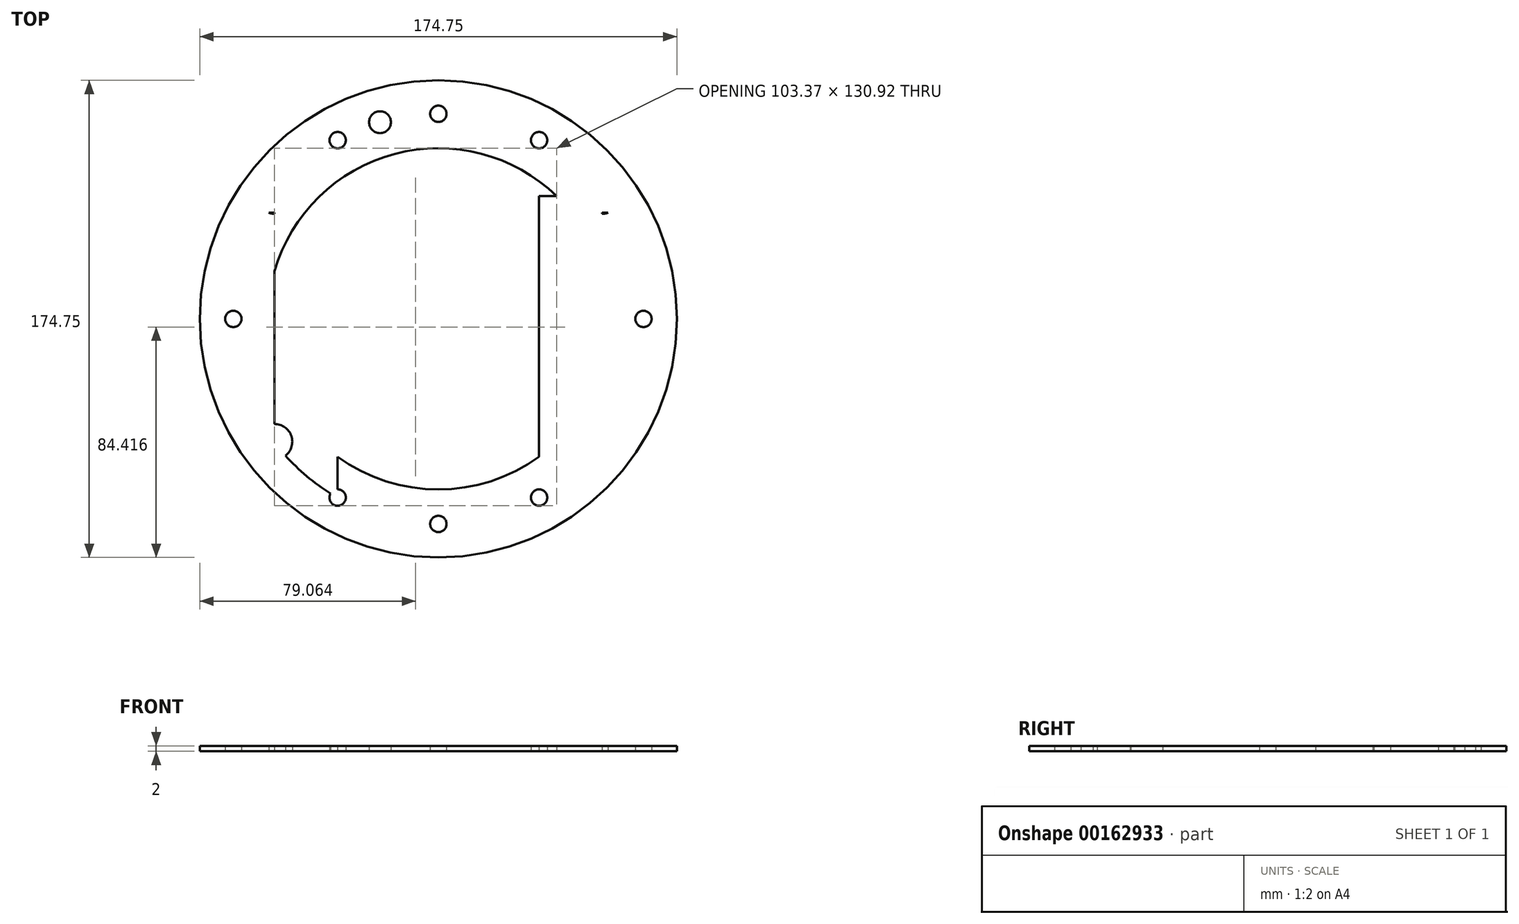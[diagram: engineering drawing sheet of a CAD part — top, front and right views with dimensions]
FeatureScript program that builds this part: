
annotation { "Feature Type Name" : "Feature", "Feature Type Description" : "" }
export const myFeature = defineFeature(function(context is Context, id is Id, definition is map)
    precondition{}
    {
        {
            var Q0;
            Q0=qCreatedBy(makeId("Top.planeOp"),FACE);
            var sketch = newSketch(context, id + "F0", { "sketchPlane" : qUnion([Q0])});
            skLineSegment(sketch, "E0.bottom", {"start": v(60.27, 43.84) * mm, "end": v(-59.73, 43.84) * mm});
            skLineSegment(sketch, "E0.top", {"start": v(60.27, -46.16) * mm, "end": v(-59.73, -46.16) * mm});
            skLineSegment(sketch, "E0.left", {"start": v(60.27, 43.84) * mm, "end": v(60.27, -46.16) * mm});
            skLineSegment(sketch, "E0.right", {"start": v(-59.73, 43.84) * mm, "end": v(-59.73, -46.16) * mm});
            skPoint(sketch, "E0.middle", {"position": v(0.27, -1.16) * mm});
            skCircle(sketch, "E1", {"center": v(60.27, 43.84) * mm, "radius": 6.5 * mm});
            skCircle(sketch, "E2", {"center": v(-59.73, 43.84) * mm, "radius": 6.5 * mm});
            skCircle(sketch, "E3", {"center": v(60.27, -46.16) * mm, "radius": 6.5 * mm});
            skCircle(sketch, "E4", {"center": v(-59.73, -46.16) * mm, "radius": 6.5 * mm});
            skCircle(sketch, "E5", {"center": v(0.27, -1.16) * mm, "radius": 87.38 * mm});
            skLineSegment(sketch, "E6.bottom", {"start": v(58.16, 49.99) * mm, "end": v(62.37, 49.99) * mm});
            skLineSegment(sketch, "E6.top", {"start": v(58.16, 37.69) * mm, "end": v(62.37, 37.69) * mm});
            skLineSegment(sketch, "E6.left", {"start": v(58.16, 49.99) * mm, "end": v(58.16, 37.69) * mm});
            skLineSegment(sketch, "E6.right", {"start": v(62.37, 49.99) * mm, "end": v(62.37, 37.69) * mm});
            skLineSegment(sketch, "E7.bottom", {"start": v(-61.84, 49.99) * mm, "end": v(-57.63, 49.99) * mm});
            skLineSegment(sketch, "E7.top", {"start": v(-61.84, 37.69) * mm, "end": v(-57.63, 37.69) * mm});
            skLineSegment(sketch, "E7.left", {"start": v(-61.84, 49.99) * mm, "end": v(-61.84, 37.69) * mm});
            skLineSegment(sketch, "E7.right", {"start": v(-57.63, 49.99) * mm, "end": v(-57.63, 37.69) * mm});
            skLineSegment(sketch, "E8.bottom", {"start": v(62.37, -40.01) * mm, "end": v(58.16, -40.01) * mm});
            skLineSegment(sketch, "E8.top", {"start": v(62.37, -52.31) * mm, "end": v(58.16, -52.31) * mm});
            skLineSegment(sketch, "E8.left", {"start": v(62.37, -40.01) * mm, "end": v(62.37, -52.31) * mm});
            skLineSegment(sketch, "E8.right", {"start": v(58.16, -40.01) * mm, "end": v(58.16, -52.31) * mm});
            skLineSegment(sketch, "E9.bottom", {"start": v(-61.84, -40.01) * mm, "end": v(-57.63, -40.01) * mm});
            skLineSegment(sketch, "E9.top", {"start": v(-61.84, -52.31) * mm, "end": v(-57.63, -52.31) * mm});
            skLineSegment(sketch, "E9.left", {"start": v(-61.84, -40.01) * mm, "end": v(-61.84, -52.31) * mm});
            skLineSegment(sketch, "E9.right", {"start": v(-57.63, -40.01) * mm, "end": v(-57.63, -52.31) * mm});
            skLineSegment(sketch, "E10.bottom", {"start": v(58.16, -40.01) * mm, "end": v(80.94, -40.01) * mm});
            skLineSegment(sketch, "E10.top", {"start": v(58.16, -52.31) * mm, "end": v(80.94, -52.31) * mm});
            skLineSegment(sketch, "E10.right", {"start": v(80.94, -40.01) * mm, "end": v(80.94, -52.31) * mm});
            skLineSegment(sketch, "E11.bottom", {"start": v(58.16, 49.99) * mm, "end": v(78.53, 49.99) * mm});
            skLineSegment(sketch, "E11.top", {"start": v(58.16, 37.69) * mm, "end": v(78.53, 37.69) * mm});
            skLineSegment(sketch, "E11.right", {"start": v(78.53, 49.99) * mm, "end": v(78.53, 37.69) * mm});
            skLineSegment(sketch, "E12.bottom", {"start": v(-57.63, 49.99) * mm, "end": v(-78, 49.99) * mm});
            skLineSegment(sketch, "E12.top", {"start": v(-57.63, 37.69) * mm, "end": v(-78, 37.69) * mm});
            skLineSegment(sketch, "E12.right", {"start": v(-78, 49.99) * mm, "end": v(-78, 37.69) * mm});
            skLineSegment(sketch, "E13.bottom", {"start": v(-57.63, -40.01) * mm, "end": v(-78, -40.01) * mm});
            skLineSegment(sketch, "E13.top", {"start": v(-57.63, -52.31) * mm, "end": v(-78, -52.31) * mm});
            skLineSegment(sketch, "E13.right", {"start": v(-78, -40.01) * mm, "end": v(-78, -52.31) * mm});
            skCircle(sketch, "E14", {"center": v(0.27, 73.95) * mm, "radius": 3 * mm});
            skCircle(sketch, "E15", {"center": v(0.27, -76.28) * mm, "radius": 3 * mm});
            skCircle(sketch, "E16", {"center": v(75.38, -1.16) * mm, "radius": 3 * mm});
            skCircle(sketch, "E17", {"center": v(-74.85, -1.16) * mm, "radius": 3 * mm});
            skCircle(sketch, "E18", {"center": v(-21.11, 70.87) * mm, "radius": 4 * mm});
            skCircle(sketch, "E19", {"center": v(0.27, -1.16) * mm, "radius": 75.13 * mm});
            skLineSegment(sketch, "E20.bottom", {"start": v(37.16, 64.3) * mm, "end": v(-36.63, 64.3) * mm});
            skLineSegment(sketch, "E20.top", {"start": v(37.16, -66.61) * mm, "end": v(-36.63, -66.61) * mm});
            skLineSegment(sketch, "E20.left", {"start": v(37.16, 64.3) * mm, "end": v(37.16, -66.61) * mm});
            skLineSegment(sketch, "E20.right", {"start": v(-36.63, 64.3) * mm, "end": v(-36.63, -66.61) * mm});
            skCircle(sketch, "E21", {"center": v(-36.63, 64.3) * mm, "radius": 3 * mm});
            skCircle(sketch, "E22", {"center": v(37.16, 64.3) * mm, "radius": 3 * mm});
            skCircle(sketch, "E23", {"center": v(37.16, -66.61) * mm, "radius": 3 * mm});
            skCircle(sketch, "E24", {"center": v(-36.63, -66.61) * mm, "radius": 3 * mm});
            skCircle(sketch, "E25", {"center": v(0.27, -1.16) * mm, "radius": 62.5 * mm});
            skSolve(sketch);
        }
        {
            var Q0;
            {var subQ0=sQuery(id+"F0.wireOp",EDGE,"E11.bottom");var subQ3=sQuery(id+"F0.wireOp",EDGE,"E5");var subQ4=makeQuery(id+"F0.imprint","INTERSECT",VERTEX,{"derivedFrom":[subQ3,subQ0]});Q0=makeQuery(id+"F0.imprint","IMPRINT",FACE,{"disambiguationData":[TD([[makeQuery(id+"F0.imprint","IMPRINT",EDGE,{"disambiguationData":[TD([[subQ4,-1.0]])],"derivedFrom":subQ3}),1.0]])]});}
            var Q1;
            {var subQ0=sQuery(id+"F0.wireOp",EDGE,"E19");var subQ1=sQuery(id+"F0.wireOp",EDGE,"E14");var subQ5=makeQuery(id+"F0.imprint","INTERSECT",VERTEX,{"disambiguationData":[OD(0.0)],"derivedFrom":[subQ1,subQ0]});Q1=makeQuery(id+"F0.imprint","IMPRINT",FACE,{"disambiguationData":[TD([[makeQuery(id+"F0.imprint","IMPRINT",EDGE,{"disambiguationData":[TD([[subQ5,1.0]])],"derivedFrom":subQ1}),-1.0]])]});}
            var Q2;
            {var subQ0=sQuery(id+"F0.wireOp",EDGE,"E20.left");var subQ1=sQuery(id+"F0.wireOp",EDGE,"b08183dc-c876-4888-9f75-b60d98332972");var subQ2=makeQuery(id+"F0.imprint","INTERSECT",VERTEX,{"disambiguationData":[OD(0.0)],"derivedFrom":[subQ1,subQ0]});Q2=makeQuery(id+"F0.imprint","IMPRINT",FACE,{"disambiguationData":[TD([[makeQuery(id+"F0.imprint","IMPRINT",EDGE,{"disambiguationData":[TD([[subQ2,-1.0]])],"derivedFrom":subQ1}),-1.0]])]});}
            var Q3;
            {var subQ1=sQuery(id+"F0.wireOp",EDGE,"E1");var subQ6=sQuery(id+"F0.wireOp",EDGE,"E0.bottom");var subQ10=makeQuery(id+"F0.imprint","INTERSECT",VERTEX,{"derivedFrom":[subQ6,subQ1]});Q3=makeQuery(id+"F0.imprint","IMPRINT",FACE,{"disambiguationData":[TD([[makeQuery(id+"F0.imprint","IMPRINT",EDGE,{"disambiguationData":[TD([[subQ10,-1.0]])],"derivedFrom":subQ6}),-1.0]])]});}
            var Q4;
            {var subQ0=sQuery(id+"F0.wireOp",EDGE,"b08183dc-c876-4888-9f75-b60d98332972");var subQ1=sQuery(id+"F0.wireOp",EDGE,"E0.bottom");var subQ2=makeQuery(id+"F0.imprint","INTERSECT",VERTEX,{"disambiguationData":[OD(1.0)],"derivedFrom":[subQ1,subQ0]});Q4=makeQuery(id+"F0.imprint","IMPRINT",FACE,{"disambiguationData":[TD([[makeQuery(id+"F0.imprint","IMPRINT",EDGE,{"disambiguationData":[TD([[subQ2,-1.0]])],"derivedFrom":subQ1}),-1.0]])]});}
            var Q5;
            {var subQ3=sQuery(id+"F0.wireOp",EDGE,"E0.right");var subQ5=sQuery(id+"F0.wireOp",EDGE,"E2");var subQ6=makeQuery(id+"F0.imprint","INTERSECT",VERTEX,{"derivedFrom":[subQ3,subQ5]});Q5=makeQuery(id+"F0.imprint","IMPRINT",FACE,{"disambiguationData":[TD([[makeQuery(id+"F0.imprint","IMPRINT",EDGE,{"disambiguationData":[TD([[subQ6,-1.0]])],"derivedFrom":subQ3}),-1.0]])]});}
            var Q6;
            {var subQ2=sQuery(id+"F0.wireOp",EDGE,"E0.bottom");var subQ6=sQuery(id+"F0.wireOp",EDGE,"b08183dc-c876-4888-9f75-b60d98332972");var subQ8=makeQuery(id+"F0.imprint","INTERSECT",VERTEX,{"disambiguationData":[OD(1.0)],"derivedFrom":[subQ2,subQ6]});Q6=makeQuery(id+"F0.imprint","IMPRINT",FACE,{"disambiguationData":[TD([[makeQuery(id+"F0.imprint","IMPRINT",EDGE,{"disambiguationData":[TD([[subQ8,-1.0]])],"derivedFrom":subQ2}),1.0]])]});}
            var Q7;
            {var subQ3=sQuery(id+"F0.wireOp",EDGE,"E19");var subQ7=sQuery(id+"F0.wireOp",EDGE,"E2");var subQ9=makeQuery(id+"F0.imprint","INTERSECT",VERTEX,{"disambiguationData":[OD(1.0)],"derivedFrom":[subQ7,subQ3]});Q7=makeQuery(id+"F0.imprint","IMPRINT",FACE,{"disambiguationData":[TD([[makeQuery(id+"F0.imprint","IMPRINT",EDGE,{"disambiguationData":[TD([[subQ9,-1.0]])],"derivedFrom":subQ3}),-1.0]])]});}
            var Q8;
            {var subQ1=sQuery(id+"F0.wireOp",EDGE,"E2");var subQ3=sQuery(id+"F0.wireOp",EDGE,"E19");var subQ4=makeQuery(id+"F0.imprint","INTERSECT",VERTEX,{"disambiguationData":[OD(1.0)],"derivedFrom":[subQ1,subQ3]});Q8=makeQuery(id+"F0.imprint","IMPRINT",FACE,{"disambiguationData":[TD([[makeQuery(id+"F0.imprint","IMPRINT",EDGE,{"disambiguationData":[TD([[subQ4,1.0]])],"derivedFrom":subQ3}),-1.0]])]});}
            var Q9;
            {var subQ1=sQuery(id+"F0.wireOp",EDGE,"E7.left");var subQ4=sQuery(id+"F0.wireOp",EDGE,"E19");var subQ5=makeQuery(id+"F0.imprint","INTERSECT",VERTEX,{"derivedFrom":[subQ1,subQ4]});Q9=makeQuery(id+"F0.imprint","IMPRINT",FACE,{"disambiguationData":[TD([[makeQuery(id+"F0.imprint","IMPRINT",EDGE,{"disambiguationData":[TD([[subQ5,1.0]])],"derivedFrom":subQ4}),-1.0]])]});}
            var Q10;
            {var subQ0=sQuery(id+"F0.wireOp",EDGE,"E2");var subQ1=sQuery(id+"F0.wireOp",EDGE,"E0.bottom");var subQ2=makeQuery(id+"F0.imprint","INTERSECT",VERTEX,{"derivedFrom":[subQ1,subQ0]});Q10=makeQuery(id+"F0.imprint","IMPRINT",FACE,{"disambiguationData":[TD([[makeQuery(id+"F0.imprint","IMPRINT",EDGE,{"disambiguationData":[TD([[subQ2,-1.0]])],"derivedFrom":subQ1}),-1.0]])]});}
            var Q11;
            {var subQ1=sQuery(id+"F0.wireOp",EDGE,"E2");var subQ3=sQuery(id+"F0.wireOp",EDGE,"E19");var subQ4=makeQuery(id+"F0.imprint","INTERSECT",VERTEX,{"disambiguationData":[OD(0.0)],"derivedFrom":[subQ1,subQ3]});Q11=makeQuery(id+"F0.imprint","IMPRINT",FACE,{"disambiguationData":[TD([[makeQuery(id+"F0.imprint","IMPRINT",EDGE,{"disambiguationData":[TD([[subQ4,-1.0]])],"derivedFrom":subQ3}),-1.0]])]});}
            var Q12;
            {var subQ0=sQuery(id+"F0.wireOp",EDGE,"E12.bottom");var subQ1=sQuery(id+"F0.wireOp",EDGE,"E2");var subQ2=makeQuery(id+"F0.imprint","INTERSECT",VERTEX,{"derivedFrom":[subQ1,sQuery(id+"F0.wireOp",EDGE,"E7.left"),subQ0]});Q12=makeQuery(id+"F0.imprint","IMPRINT",FACE,{"disambiguationData":[TD([[makeQuery(id+"F0.imprint","IMPRINT",EDGE,{"disambiguationData":[TD([[subQ2,1.0]])],"derivedFrom":subQ1}),1.0]])]});}
            var Q13;
            {var subQ3=sQuery(id+"F0.wireOp",EDGE,"E0.right");var subQ9=sQuery(id+"F0.wireOp",EDGE,"E0.bottom");var subQ10=makeQuery(id+"F0.imprint","INTERSECT",VERTEX,{"derivedFrom":[subQ9,subQ3]});Q13=makeQuery(id+"F0.imprint","IMPRINT",FACE,{"disambiguationData":[TD([[makeQuery(id+"F0.imprint","IMPRINT",EDGE,{"disambiguationData":[TD([[subQ10,1.0]])],"derivedFrom":subQ9}),-1.0]])]});}
            var Q14;
            {var subQ0=sQuery(id+"F0.wireOp",EDGE,"E0.right");var subQ1=sQuery(id+"F0.wireOp",EDGE,"E0.bottom");var subQ2=makeQuery(id+"F0.imprint","INTERSECT",VERTEX,{"derivedFrom":[subQ1,subQ0]});Q14=makeQuery(id+"F0.imprint","IMPRINT",FACE,{"disambiguationData":[TD([[makeQuery(id+"F0.imprint","IMPRINT",EDGE,{"disambiguationData":[TD([[subQ2,1.0]])],"derivedFrom":subQ1}),1.0]])]});}
            var Q15;
            {var subQ0=sQuery(id+"F0.wireOp",EDGE,"E2");var subQ1=sQuery(id+"F0.wireOp",EDGE,"E0.bottom");var subQ2=makeQuery(id+"F0.imprint","INTERSECT",VERTEX,{"derivedFrom":[subQ1,subQ0]});Q15=makeQuery(id+"F0.imprint","IMPRINT",FACE,{"disambiguationData":[TD([[makeQuery(id+"F0.imprint","IMPRINT",EDGE,{"disambiguationData":[TD([[subQ2,-1.0]])],"derivedFrom":subQ1}),1.0]])]});}
            var Q16;
            {var subQ0=sQuery(id+"F0.wireOp",EDGE,"E12.top");var subQ1=sQuery(id+"F0.wireOp",EDGE,"E0.right");var subQ2=makeQuery(id+"F0.imprint","INTERSECT",VERTEX,{"derivedFrom":[subQ1,subQ0]});Q16=makeQuery(id+"F0.imprint","IMPRINT",FACE,{"disambiguationData":[TD([[makeQuery(id+"F0.imprint","IMPRINT",EDGE,{"disambiguationData":[TD([[subQ2,-1.0]])],"derivedFrom":subQ1}),1.0]])]});}
            var Q17;
            {var subQ0=sQuery(id+"F0.wireOp",EDGE,"E12.top");var subQ1=sQuery(id+"F0.wireOp",EDGE,"E0.right");var subQ2=makeQuery(id+"F0.imprint","INTERSECT",VERTEX,{"derivedFrom":[subQ1,subQ0]});Q17=makeQuery(id+"F0.imprint","IMPRINT",FACE,{"disambiguationData":[TD([[makeQuery(id+"F0.imprint","IMPRINT",EDGE,{"disambiguationData":[TD([[subQ2,-1.0]])],"derivedFrom":subQ1}),-1.0]])]});}
            var Q18;
            {var subQ1=sQuery(id+"F0.wireOp",EDGE,"E2");var subQ3=sQuery(id+"F0.wireOp",EDGE,"E19");var subQ4=makeQuery(id+"F0.imprint","INTERSECT",VERTEX,{"disambiguationData":[OD(1.0)],"derivedFrom":[subQ1,subQ3]});Q18=makeQuery(id+"F0.imprint","IMPRINT",FACE,{"disambiguationData":[TD([[makeQuery(id+"F0.imprint","IMPRINT",EDGE,{"disambiguationData":[TD([[subQ4,1.0]])],"derivedFrom":subQ3}),1.0]])]});}
            var Q19;
            {var subQ1=sQuery(id+"F0.wireOp",EDGE,"E2");var subQ3=sQuery(id+"F0.wireOp",EDGE,"E19");var subQ4=makeQuery(id+"F0.imprint","INTERSECT",VERTEX,{"disambiguationData":[OD(1.0)],"derivedFrom":[subQ1,subQ3]});Q19=makeQuery(id+"F0.imprint","IMPRINT",FACE,{"disambiguationData":[TD([[makeQuery(id+"F0.imprint","IMPRINT",EDGE,{"disambiguationData":[TD([[subQ4,-1.0]])],"derivedFrom":subQ3}),1.0]])]});}
            var Q20;
            {var subQ0=sQuery(id+"F0.wireOp",EDGE,"E13.right");var subQ1=sQuery(id+"F0.wireOp",EDGE,"E13.bottom");var subQ2=makeQuery(id+"F0.imprint","INTERSECT",VERTEX,{"derivedFrom":[subQ1,subQ0]});Q20=makeQuery(id+"F0.imprint","IMPRINT",FACE,{"disambiguationData":[TD([[makeQuery(id+"F0.imprint","IMPRINT",EDGE,{"disambiguationData":[TD([[subQ2,1.0]])],"derivedFrom":subQ1}),-1.0]])]});}
            var Q21;
            {var subQ0=sQuery(id+"F0.wireOp",EDGE,"E11.bottom");var subQ1=sQuery(id+"F0.wireOp",EDGE,"E1");var subQ2=makeQuery(id+"F0.imprint","INTERSECT",VERTEX,{"derivedFrom":[subQ1,sQuery(id+"F0.wireOp",EDGE,"E6.right"),subQ0]});Q21=makeQuery(id+"F0.imprint","IMPRINT",FACE,{"disambiguationData":[TD([[makeQuery(id+"F0.imprint","IMPRINT",EDGE,{"disambiguationData":[TD([[subQ2,-1.0]])],"derivedFrom":subQ1}),1.0]])]});}
            var Q22;
            {var subQ1=sQuery(id+"F0.wireOp",EDGE,"E1");var subQ3=sQuery(id+"F0.wireOp",EDGE,"E19");var subQ4=makeQuery(id+"F0.imprint","INTERSECT",VERTEX,{"disambiguationData":[OD(0.0)],"derivedFrom":[subQ1,subQ3]});Q22=makeQuery(id+"F0.imprint","IMPRINT",FACE,{"disambiguationData":[TD([[makeQuery(id+"F0.imprint","IMPRINT",EDGE,{"disambiguationData":[TD([[subQ4,1.0]])],"derivedFrom":subQ3}),-1.0]])]});}
            var Q23;
            {var subQ0=sQuery(id+"F0.wireOp",EDGE,"E6.left");var subQ1=sQuery(id+"F0.wireOp",EDGE,"E0.bottom");var subQ2=makeQuery(id+"F0.imprint","INTERSECT",VERTEX,{"derivedFrom":[subQ1,subQ0]});Q23=makeQuery(id+"F0.imprint","IMPRINT",FACE,{"disambiguationData":[TD([[makeQuery(id+"F0.imprint","IMPRINT",EDGE,{"disambiguationData":[TD([[subQ2,-1.0]])],"derivedFrom":subQ1}),-1.0]])]});}
            var Q24;
            {var subQ0=sQuery(id+"F0.wireOp",EDGE,"E6.left");var subQ1=sQuery(id+"F0.wireOp",EDGE,"E0.bottom");var subQ2=makeQuery(id+"F0.imprint","INTERSECT",VERTEX,{"derivedFrom":[subQ1,subQ0]});Q24=makeQuery(id+"F0.imprint","IMPRINT",FACE,{"disambiguationData":[TD([[makeQuery(id+"F0.imprint","IMPRINT",EDGE,{"disambiguationData":[TD([[subQ2,-1.0]])],"derivedFrom":subQ1}),1.0]])]});}
            var Q25;
            {var subQ3=sQuery(id+"F0.wireOp",EDGE,"E0.left");var subQ7=sQuery(id+"F0.wireOp",EDGE,"E0.bottom");var subQ8=makeQuery(id+"F0.imprint","INTERSECT",VERTEX,{"derivedFrom":[subQ7,subQ3]});Q25=makeQuery(id+"F0.imprint","IMPRINT",FACE,{"disambiguationData":[TD([[makeQuery(id+"F0.imprint","IMPRINT",EDGE,{"disambiguationData":[TD([[subQ8,-1.0]])],"derivedFrom":subQ7}),-1.0]])]});}
            var Q26;
            {var subQ0=sQuery(id+"F0.wireOp",EDGE,"E0.left");var subQ1=sQuery(id+"F0.wireOp",EDGE,"E0.bottom");var subQ2=makeQuery(id+"F0.imprint","INTERSECT",VERTEX,{"derivedFrom":[subQ1,subQ0]});Q26=makeQuery(id+"F0.imprint","IMPRINT",FACE,{"disambiguationData":[TD([[makeQuery(id+"F0.imprint","IMPRINT",EDGE,{"disambiguationData":[TD([[subQ2,-1.0]])],"derivedFrom":subQ1}),1.0]])]});}
            var Q27;
            {var subQ1=sQuery(id+"F0.wireOp",EDGE,"E6.right");var subQ4=sQuery(id+"F0.wireOp",EDGE,"E19");var subQ5=makeQuery(id+"F0.imprint","INTERSECT",VERTEX,{"derivedFrom":[subQ1,subQ4]});Q27=makeQuery(id+"F0.imprint","IMPRINT",FACE,{"disambiguationData":[TD([[makeQuery(id+"F0.imprint","IMPRINT",EDGE,{"disambiguationData":[TD([[subQ5,-1.0]])],"derivedFrom":subQ4}),-1.0]])]});}
            var Q28;
            {var subQ1=sQuery(id+"F0.wireOp",EDGE,"E1");var subQ3=sQuery(id+"F0.wireOp",EDGE,"E19");var subQ4=makeQuery(id+"F0.imprint","INTERSECT",VERTEX,{"disambiguationData":[OD(1.0)],"derivedFrom":[subQ1,subQ3]});Q28=makeQuery(id+"F0.imprint","IMPRINT",FACE,{"disambiguationData":[TD([[makeQuery(id+"F0.imprint","IMPRINT",EDGE,{"disambiguationData":[TD([[subQ4,-1.0]])],"derivedFrom":subQ3}),-1.0]])]});}
            var Q29;
            {var subQ1=sQuery(id+"F0.wireOp",EDGE,"E1");var subQ3=sQuery(id+"F0.wireOp",EDGE,"E19");var subQ4=makeQuery(id+"F0.imprint","INTERSECT",VERTEX,{"disambiguationData":[OD(1.0)],"derivedFrom":[subQ1,subQ3]});Q29=makeQuery(id+"F0.imprint","IMPRINT",FACE,{"disambiguationData":[TD([[makeQuery(id+"F0.imprint","IMPRINT",EDGE,{"disambiguationData":[TD([[subQ4,-1.0]])],"derivedFrom":subQ3}),1.0]])]});}
            var Q30;
            {var subQ0=sQuery(id+"F0.wireOp",EDGE,"E11.top");var subQ1=sQuery(id+"F0.wireOp",EDGE,"E0.left");var subQ2=makeQuery(id+"F0.imprint","INTERSECT",VERTEX,{"derivedFrom":[subQ1,subQ0]});Q30=makeQuery(id+"F0.imprint","IMPRINT",FACE,{"disambiguationData":[TD([[makeQuery(id+"F0.imprint","IMPRINT",EDGE,{"disambiguationData":[TD([[subQ2,-1.0]])],"derivedFrom":subQ1}),1.0]])]});}
            var Q31;
            {var subQ0=sQuery(id+"F0.wireOp",EDGE,"E11.top");var subQ1=sQuery(id+"F0.wireOp",EDGE,"E0.left");var subQ2=makeQuery(id+"F0.imprint","INTERSECT",VERTEX,{"derivedFrom":[subQ1,subQ0]});Q31=makeQuery(id+"F0.imprint","IMPRINT",FACE,{"disambiguationData":[TD([[makeQuery(id+"F0.imprint","IMPRINT",EDGE,{"disambiguationData":[TD([[subQ2,-1.0]])],"derivedFrom":subQ1}),-1.0]])]});}
            var Q32;
            {var subQ1=sQuery(id+"F0.wireOp",EDGE,"E1");var subQ3=sQuery(id+"F0.wireOp",EDGE,"E19");var subQ4=makeQuery(id+"F0.imprint","INTERSECT",VERTEX,{"disambiguationData":[OD(1.0)],"derivedFrom":[subQ1,subQ3]});Q32=makeQuery(id+"F0.imprint","IMPRINT",FACE,{"disambiguationData":[TD([[makeQuery(id+"F0.imprint","IMPRINT",EDGE,{"disambiguationData":[TD([[subQ4,1.0]])],"derivedFrom":subQ3}),1.0]])]});}
            var Q33;
            {var subQ1=sQuery(id+"F0.wireOp",EDGE,"E1");var subQ7=sQuery(id+"F0.wireOp",EDGE,"E19");var subQ9=makeQuery(id+"F0.imprint","INTERSECT",VERTEX,{"disambiguationData":[OD(1.0)],"derivedFrom":[subQ1,subQ7]});Q33=makeQuery(id+"F0.imprint","IMPRINT",FACE,{"disambiguationData":[TD([[makeQuery(id+"F0.imprint","IMPRINT",EDGE,{"disambiguationData":[TD([[subQ9,1.0]])],"derivedFrom":subQ7}),-1.0]])]});}
            var Q34;
            {var subQ0=sQuery(id+"F0.wireOp",EDGE,"E1");var subQ4=sQuery(id+"F0.wireOp",EDGE,"E0.bottom");var subQ5=makeQuery(id+"F0.imprint","INTERSECT",VERTEX,{"derivedFrom":[subQ4,subQ0]});Q34=makeQuery(id+"F0.imprint","IMPRINT",FACE,{"disambiguationData":[TD([[makeQuery(id+"F0.imprint","IMPRINT",EDGE,{"disambiguationData":[TD([[subQ5,-1.0]])],"derivedFrom":subQ4}),1.0]])]});}
            var Q35;
            {var subQ3=sQuery(id+"F0.wireOp",EDGE,"E0.left");var subQ6=sQuery(id+"F0.wireOp",EDGE,"E1");var subQ8=makeQuery(id+"F0.imprint","INTERSECT",VERTEX,{"derivedFrom":[subQ3,subQ6]});Q35=makeQuery(id+"F0.imprint","IMPRINT",FACE,{"disambiguationData":[TD([[makeQuery(id+"F0.imprint","IMPRINT",EDGE,{"disambiguationData":[TD([[subQ8,-1.0]])],"derivedFrom":subQ3}),1.0]])]});}
            var Q36;
            {var subQ5=sQuery(id+"F0.wireOp",EDGE,"E5");var subQ8=sQuery(id+"F0.wireOp",EDGE,"E10.bottom");var subQ9=makeQuery(id+"F0.imprint","INTERSECT",VERTEX,{"derivedFrom":[subQ5,subQ8]});Q36=makeQuery(id+"F0.imprint","IMPRINT",FACE,{"disambiguationData":[TD([[makeQuery(id+"F0.imprint","IMPRINT",EDGE,{"disambiguationData":[TD([[subQ9,1.0]])],"derivedFrom":subQ8}),1.0]])]});}
            var Q37;
            {var subQ2=sQuery(id+"F0.wireOp",EDGE,"E0.top");var subQ6=sQuery(id+"F0.wireOp",EDGE,"b08183dc-c876-4888-9f75-b60d98332972");var subQ8=makeQuery(id+"F0.imprint","INTERSECT",VERTEX,{"disambiguationData":[OD(1.0)],"derivedFrom":[subQ2,subQ6]});Q37=makeQuery(id+"F0.imprint","IMPRINT",FACE,{"disambiguationData":[TD([[makeQuery(id+"F0.imprint","IMPRINT",EDGE,{"disambiguationData":[TD([[subQ8,-1.0]])],"derivedFrom":subQ2}),-1.0]])]});}
            var Q38;
            {var subQ0=sQuery(id+"F0.wireOp",EDGE,"b08183dc-c876-4888-9f75-b60d98332972");var subQ1=sQuery(id+"F0.wireOp",EDGE,"E0.top");var subQ2=makeQuery(id+"F0.imprint","INTERSECT",VERTEX,{"disambiguationData":[OD(1.0)],"derivedFrom":[subQ1,subQ0]});Q38=makeQuery(id+"F0.imprint","IMPRINT",FACE,{"disambiguationData":[TD([[makeQuery(id+"F0.imprint","IMPRINT",EDGE,{"disambiguationData":[TD([[subQ2,-1.0]])],"derivedFrom":subQ1}),1.0]])]});}
            var Q39;
            {var subQ1=sQuery(id+"F0.wireOp",EDGE,"b08183dc-c876-4888-9f75-b60d98332972");var subQ5=sQuery(id+"F0.wireOp",EDGE,"E20.right");var subQ6=makeQuery(id+"F0.imprint","INTERSECT",VERTEX,{"disambiguationData":[OD(1.0)],"derivedFrom":[subQ1,subQ5]});Q39=makeQuery(id+"F0.imprint","IMPRINT",FACE,{"disambiguationData":[TD([[makeQuery(id+"F0.imprint","IMPRINT",EDGE,{"disambiguationData":[TD([[subQ6,-1.0]])],"derivedFrom":subQ1}),-1.0]])]});}
            var Q40;
            {var subQ1=sQuery(id+"F0.wireOp",EDGE,"E3");var subQ6=sQuery(id+"F0.wireOp",EDGE,"E0.top");var subQ10=makeQuery(id+"F0.imprint","INTERSECT",VERTEX,{"derivedFrom":[subQ6,subQ1]});Q40=makeQuery(id+"F0.imprint","IMPRINT",FACE,{"disambiguationData":[TD([[makeQuery(id+"F0.imprint","IMPRINT",EDGE,{"disambiguationData":[TD([[subQ10,-1.0]])],"derivedFrom":subQ6}),1.0]])]});}
            var Q41;
            {var subQ0=sQuery(id+"F0.wireOp",EDGE,"E3");var subQ2=sQuery(id+"F0.wireOp",EDGE,"E0.top");var subQ3=makeQuery(id+"F0.imprint","INTERSECT",VERTEX,{"derivedFrom":[subQ2,subQ0]});Q41=makeQuery(id+"F0.imprint","IMPRINT",FACE,{"disambiguationData":[TD([[makeQuery(id+"F0.imprint","IMPRINT",EDGE,{"disambiguationData":[TD([[subQ3,-1.0]])],"derivedFrom":subQ2}),-1.0]])]});}
            var Q42;
            {var subQ13=sQuery(id+"F0.wireOp",EDGE,"E13.top");var subQ15=sQuery(id+"F0.wireOp",EDGE,"E5");var subQ16=makeQuery(id+"F0.imprint","INTERSECT",VERTEX,{"derivedFrom":[subQ15,subQ13]});Q42=makeQuery(id+"F0.imprint","IMPRINT",FACE,{"disambiguationData":[TD([[makeQuery(id+"F0.imprint","IMPRINT",EDGE,{"disambiguationData":[TD([[subQ16,-1.0]])],"derivedFrom":subQ15}),1.0]])]});}
            var Q43;
            {var subQ5=sQuery(id+"F0.wireOp",EDGE,"E19");var subQ7=sQuery(id+"F0.wireOp",EDGE,"E15");var subQ10=makeQuery(id+"F0.imprint","INTERSECT",VERTEX,{"disambiguationData":[OD(0.0)],"derivedFrom":[subQ7,subQ5]});Q43=makeQuery(id+"F0.imprint","IMPRINT",FACE,{"disambiguationData":[TD([[makeQuery(id+"F0.imprint","IMPRINT",EDGE,{"disambiguationData":[TD([[subQ10,1.0]])],"derivedFrom":subQ7}),-1.0]])]});}
            var Q44;
            {var subQ3=sQuery(id+"F0.wireOp",EDGE,"E5");var subQ5=sQuery(id+"F0.wireOp",EDGE,"E13.right");var subQ6=makeQuery(id+"F0.imprint","INTERSECT",VERTEX,{"derivedFrom":[subQ3,subQ5]});Q44=makeQuery(id+"F0.imprint","IMPRINT",FACE,{"disambiguationData":[TD([[makeQuery(id+"F0.imprint","IMPRINT",EDGE,{"disambiguationData":[TD([[subQ6,-1.0]])],"derivedFrom":subQ3}),1.0]])]});}
            var Q45;
            {var subQ1=sQuery(id+"F0.wireOp",EDGE,"E4");var subQ3=sQuery(id+"F0.wireOp",EDGE,"E19");var subQ4=makeQuery(id+"F0.imprint","INTERSECT",VERTEX,{"disambiguationData":[OD(0.0)],"derivedFrom":[subQ1,subQ3]});Q45=makeQuery(id+"F0.imprint","IMPRINT",FACE,{"disambiguationData":[TD([[makeQuery(id+"F0.imprint","IMPRINT",EDGE,{"disambiguationData":[TD([[subQ4,-1.0]])],"derivedFrom":subQ3}),-1.0]])]});}
            var Q46;
            {var subQ1=sQuery(id+"F0.wireOp",EDGE,"E9.left");var subQ4=sQuery(id+"F0.wireOp",EDGE,"E19");var subQ5=makeQuery(id+"F0.imprint","INTERSECT",VERTEX,{"derivedFrom":[subQ1,subQ4]});Q46=makeQuery(id+"F0.imprint","IMPRINT",FACE,{"disambiguationData":[TD([[makeQuery(id+"F0.imprint","IMPRINT",EDGE,{"disambiguationData":[TD([[subQ5,-1.0]])],"derivedFrom":subQ4}),-1.0]])]});}
            var Q47;
            {var subQ0=sQuery(id+"F0.wireOp",EDGE,"E13.top");var subQ1=sQuery(id+"F0.wireOp",EDGE,"E4");var subQ2=makeQuery(id+"F0.imprint","INTERSECT",VERTEX,{"derivedFrom":[subQ1,sQuery(id+"F0.wireOp",EDGE,"E9.left"),subQ0]});Q47=makeQuery(id+"F0.imprint","IMPRINT",FACE,{"disambiguationData":[TD([[makeQuery(id+"F0.imprint","IMPRINT",EDGE,{"disambiguationData":[TD([[subQ2,-1.0]])],"derivedFrom":subQ1}),1.0]])]});}
            var Q48;
            {var subQ1=sQuery(id+"F0.wireOp",EDGE,"E4");var subQ3=sQuery(id+"F0.wireOp",EDGE,"E19");var subQ4=makeQuery(id+"F0.imprint","INTERSECT",VERTEX,{"disambiguationData":[OD(1.0)],"derivedFrom":[subQ1,subQ3]});Q48=makeQuery(id+"F0.imprint","IMPRINT",FACE,{"disambiguationData":[TD([[makeQuery(id+"F0.imprint","IMPRINT",EDGE,{"disambiguationData":[TD([[subQ4,1.0]])],"derivedFrom":subQ3}),-1.0]])]});}
            var Q49;
            {var subQ0=sQuery(id+"F0.wireOp",EDGE,"E4");var subQ1=sQuery(id+"F0.wireOp",EDGE,"E0.top");var subQ2=makeQuery(id+"F0.imprint","INTERSECT",VERTEX,{"derivedFrom":[subQ1,subQ0]});Q49=makeQuery(id+"F0.imprint","IMPRINT",FACE,{"disambiguationData":[TD([[makeQuery(id+"F0.imprint","IMPRINT",EDGE,{"disambiguationData":[TD([[subQ2,-1.0]])],"derivedFrom":subQ1}),1.0]])]});}
            var Q50;
            {var subQ0=sQuery(id+"F0.wireOp",EDGE,"E4");var subQ1=sQuery(id+"F0.wireOp",EDGE,"E0.top");var subQ2=makeQuery(id+"F0.imprint","INTERSECT",VERTEX,{"derivedFrom":[subQ1,subQ0]});Q50=makeQuery(id+"F0.imprint","IMPRINT",FACE,{"disambiguationData":[TD([[makeQuery(id+"F0.imprint","IMPRINT",EDGE,{"disambiguationData":[TD([[subQ2,-1.0]])],"derivedFrom":subQ1}),-1.0]])]});}
            var Q51;
            {var subQ0=sQuery(id+"F0.wireOp",EDGE,"E0.right");var subQ1=sQuery(id+"F0.wireOp",EDGE,"E0.top");var subQ2=makeQuery(id+"F0.imprint","INTERSECT",VERTEX,{"derivedFrom":[subQ1,subQ0]});Q51=makeQuery(id+"F0.imprint","IMPRINT",FACE,{"disambiguationData":[TD([[makeQuery(id+"F0.imprint","IMPRINT",EDGE,{"disambiguationData":[TD([[subQ2,1.0]])],"derivedFrom":subQ1}),-1.0]])]});}
            var Q52;
            {var subQ5=sQuery(id+"F0.wireOp",EDGE,"E0.right");var subQ6=sQuery(id+"F0.wireOp",EDGE,"E0.top");var subQ7=makeQuery(id+"F0.imprint","INTERSECT",VERTEX,{"derivedFrom":[subQ6,subQ5]});Q52=makeQuery(id+"F0.imprint","IMPRINT",FACE,{"disambiguationData":[TD([[makeQuery(id+"F0.imprint","IMPRINT",EDGE,{"disambiguationData":[TD([[subQ7,1.0]])],"derivedFrom":subQ6}),1.0]])]});}
            var Q53;
            {var subQ1=sQuery(id+"F0.wireOp",EDGE,"E4");var subQ3=sQuery(id+"F0.wireOp",EDGE,"E19");var subQ4=makeQuery(id+"F0.imprint","INTERSECT",VERTEX,{"disambiguationData":[OD(0.0)],"derivedFrom":[subQ1,subQ3]});Q53=makeQuery(id+"F0.imprint","IMPRINT",FACE,{"disambiguationData":[TD([[makeQuery(id+"F0.imprint","IMPRINT",EDGE,{"disambiguationData":[TD([[subQ4,-1.0]])],"derivedFrom":subQ3}),1.0]])]});}
            var Q54;
            {var subQ1=sQuery(id+"F0.wireOp",EDGE,"E4");var subQ3=sQuery(id+"F0.wireOp",EDGE,"E19");var subQ4=makeQuery(id+"F0.imprint","INTERSECT",VERTEX,{"disambiguationData":[OD(0.0)],"derivedFrom":[subQ1,subQ3]});Q54=makeQuery(id+"F0.imprint","IMPRINT",FACE,{"disambiguationData":[TD([[makeQuery(id+"F0.imprint","IMPRINT",EDGE,{"disambiguationData":[TD([[subQ4,1.0]])],"derivedFrom":subQ3}),1.0]])]});}
            var Q55;
            {var subQ0=sQuery(id+"F0.wireOp",EDGE,"E4");var subQ1=sQuery(id+"F0.wireOp",EDGE,"E0.right");var subQ2=makeQuery(id+"F0.imprint","INTERSECT",VERTEX,{"derivedFrom":[subQ1,subQ0]});Q55=makeQuery(id+"F0.imprint","IMPRINT",FACE,{"disambiguationData":[TD([[makeQuery(id+"F0.imprint","IMPRINT",EDGE,{"disambiguationData":[TD([[subQ2,-1.0]])],"derivedFrom":subQ1}),-1.0]])]});}
            var Q56;
            {var subQ0=sQuery(id+"F0.wireOp",EDGE,"E4");var subQ1=sQuery(id+"F0.wireOp",EDGE,"E0.right");var subQ2=makeQuery(id+"F0.imprint","INTERSECT",VERTEX,{"derivedFrom":[subQ1,subQ0]});Q56=makeQuery(id+"F0.imprint","IMPRINT",FACE,{"disambiguationData":[TD([[makeQuery(id+"F0.imprint","IMPRINT",EDGE,{"disambiguationData":[TD([[subQ2,-1.0]])],"derivedFrom":subQ1}),1.0]])]});}
            var Q57;
            {var subQ0=sQuery(id+"F0.wireOp",EDGE,"E10.top");var subQ3=sQuery(id+"F0.wireOp",EDGE,"E5");var subQ4=makeQuery(id+"F0.imprint","INTERSECT",VERTEX,{"derivedFrom":[subQ3,subQ0]});Q57=makeQuery(id+"F0.imprint","IMPRINT",FACE,{"disambiguationData":[TD([[makeQuery(id+"F0.imprint","IMPRINT",EDGE,{"disambiguationData":[TD([[subQ4,-1.0]])],"derivedFrom":subQ3}),1.0]])]});}
            var Q58;
            {var subQ1=sQuery(id+"F0.wireOp",EDGE,"E3");var subQ3=sQuery(id+"F0.wireOp",EDGE,"E19");var subQ4=makeQuery(id+"F0.imprint","INTERSECT",VERTEX,{"disambiguationData":[OD(0.0)],"derivedFrom":[subQ1,subQ3]});Q58=makeQuery(id+"F0.imprint","IMPRINT",FACE,{"disambiguationData":[TD([[makeQuery(id+"F0.imprint","IMPRINT",EDGE,{"disambiguationData":[TD([[subQ4,1.0]])],"derivedFrom":subQ3}),-1.0]])]});}
            var Q59;
            {var subQ1=sQuery(id+"F0.wireOp",EDGE,"E8.left");var subQ4=sQuery(id+"F0.wireOp",EDGE,"E19");var subQ5=makeQuery(id+"F0.imprint","INTERSECT",VERTEX,{"derivedFrom":[subQ1,subQ4]});Q59=makeQuery(id+"F0.imprint","IMPRINT",FACE,{"disambiguationData":[TD([[makeQuery(id+"F0.imprint","IMPRINT",EDGE,{"disambiguationData":[TD([[subQ5,1.0]])],"derivedFrom":subQ4}),-1.0]])]});}
            var Q60;
            {var subQ1=sQuery(id+"F0.wireOp",EDGE,"E3");var subQ3=sQuery(id+"F0.wireOp",EDGE,"E19");var subQ4=makeQuery(id+"F0.imprint","INTERSECT",VERTEX,{"disambiguationData":[OD(0.0)],"derivedFrom":[subQ1,subQ3]});Q60=makeQuery(id+"F0.imprint","IMPRINT",FACE,{"disambiguationData":[TD([[makeQuery(id+"F0.imprint","IMPRINT",EDGE,{"disambiguationData":[TD([[subQ4,-1.0]])],"derivedFrom":subQ3}),1.0]])]});}
            var Q61;
            {var subQ1=sQuery(id+"F0.wireOp",EDGE,"E3");var subQ3=sQuery(id+"F0.wireOp",EDGE,"E19");var subQ4=makeQuery(id+"F0.imprint","INTERSECT",VERTEX,{"disambiguationData":[OD(0.0)],"derivedFrom":[subQ1,subQ3]});Q61=makeQuery(id+"F0.imprint","IMPRINT",FACE,{"disambiguationData":[TD([[makeQuery(id+"F0.imprint","IMPRINT",EDGE,{"disambiguationData":[TD([[subQ4,1.0]])],"derivedFrom":subQ3}),1.0]])]});}
            var Q62;
            {var subQ3=sQuery(id+"F0.wireOp",EDGE,"E0.left");var subQ8=sQuery(id+"F0.wireOp",EDGE,"E0.top");var subQ11=makeQuery(id+"F0.imprint","INTERSECT",VERTEX,{"derivedFrom":[subQ8,subQ3]});Q62=makeQuery(id+"F0.imprint","IMPRINT",FACE,{"disambiguationData":[TD([[makeQuery(id+"F0.imprint","IMPRINT",EDGE,{"disambiguationData":[TD([[subQ11,-1.0]])],"derivedFrom":subQ8}),1.0]])]});}
            var Q63;
            {var subQ0=sQuery(id+"F0.wireOp",EDGE,"E3");var subQ1=sQuery(id+"F0.wireOp",EDGE,"E0.left");var subQ2=makeQuery(id+"F0.imprint","INTERSECT",VERTEX,{"derivedFrom":[subQ1,subQ0]});Q63=makeQuery(id+"F0.imprint","IMPRINT",FACE,{"disambiguationData":[TD([[makeQuery(id+"F0.imprint","IMPRINT",EDGE,{"disambiguationData":[TD([[subQ2,-1.0]])],"derivedFrom":subQ1}),1.0]])]});}
            var Q64;
            {var subQ0=sQuery(id+"F0.wireOp",EDGE,"E3");var subQ1=sQuery(id+"F0.wireOp",EDGE,"E0.left");var subQ2=makeQuery(id+"F0.imprint","INTERSECT",VERTEX,{"derivedFrom":[subQ1,subQ0]});Q64=makeQuery(id+"F0.imprint","IMPRINT",FACE,{"disambiguationData":[TD([[makeQuery(id+"F0.imprint","IMPRINT",EDGE,{"disambiguationData":[TD([[subQ2,-1.0]])],"derivedFrom":subQ1}),-1.0]])]});}
            var Q65;
            {var subQ0=sQuery(id+"F0.wireOp",EDGE,"E0.left");var subQ1=sQuery(id+"F0.wireOp",EDGE,"E0.top");var subQ2=makeQuery(id+"F0.imprint","INTERSECT",VERTEX,{"derivedFrom":[subQ1,subQ0]});Q65=makeQuery(id+"F0.imprint","IMPRINT",FACE,{"disambiguationData":[TD([[makeQuery(id+"F0.imprint","IMPRINT",EDGE,{"disambiguationData":[TD([[subQ2,-1.0]])],"derivedFrom":subQ1}),-1.0]])]});}
            var Q66;
            {var subQ0=sQuery(id+"F0.wireOp",EDGE,"E8.right");var subQ1=sQuery(id+"F0.wireOp",EDGE,"E0.top");var subQ2=makeQuery(id+"F0.imprint","INTERSECT",VERTEX,{"derivedFrom":[subQ1,subQ0]});Q66=makeQuery(id+"F0.imprint","IMPRINT",FACE,{"disambiguationData":[TD([[makeQuery(id+"F0.imprint","IMPRINT",EDGE,{"disambiguationData":[TD([[subQ2,-1.0]])],"derivedFrom":subQ1}),-1.0]])]});}
            var Q67;
            {var subQ0=sQuery(id+"F0.wireOp",EDGE,"E10.top");var subQ1=sQuery(id+"F0.wireOp",EDGE,"E3");var subQ2=makeQuery(id+"F0.imprint","INTERSECT",VERTEX,{"derivedFrom":[subQ1,sQuery(id+"F0.wireOp",EDGE,"E8.left"),subQ0]});Q67=makeQuery(id+"F0.imprint","IMPRINT",FACE,{"disambiguationData":[TD([[makeQuery(id+"F0.imprint","IMPRINT",EDGE,{"disambiguationData":[TD([[subQ2,1.0]])],"derivedFrom":subQ1}),1.0]])]});}
            var Q68;
            {var subQ0=sQuery(id+"F0.wireOp",EDGE,"E23");var subQ1=sQuery(id+"F0.wireOp",EDGE,"E20.top");var subQ2=makeQuery(id+"F0.imprint","INTERSECT",VERTEX,{"derivedFrom":[subQ1,subQ0]});Q68=makeQuery(id+"F0.imprint","IMPRINT",FACE,{"disambiguationData":[TD([[makeQuery(id+"F0.imprint","IMPRINT",EDGE,{"disambiguationData":[TD([[subQ2,-1.0]])],"derivedFrom":subQ1}),-1.0]])]});}
            var Q69;
            {var subQ1=sQuery(id+"F0.wireOp",EDGE,"E20.bottom");var subQ5=sQuery(id+"F0.wireOp",EDGE,"E22");var subQ11=makeQuery(id+"F0.imprint","INTERSECT",VERTEX,{"derivedFrom":[subQ1,subQ5]});Q69=makeQuery(id+"F0.imprint","IMPRINT",FACE,{"disambiguationData":[TD([[makeQuery(id+"F0.imprint","IMPRINT",EDGE,{"disambiguationData":[TD([[subQ11,-1.0]])],"derivedFrom":subQ1}),1.0]])]});}
            var Q70;
            {var subQ0=sQuery(id+"F0.wireOp",EDGE,"E8.right");var subQ1=sQuery(id+"F0.wireOp",EDGE,"E0.top");var subQ2=makeQuery(id+"F0.imprint","INTERSECT",VERTEX,{"derivedFrom":[subQ1,subQ0]});Q70=makeQuery(id+"F0.imprint","IMPRINT",FACE,{"disambiguationData":[TD([[makeQuery(id+"F0.imprint","IMPRINT",EDGE,{"disambiguationData":[TD([[subQ2,-1.0]])],"derivedFrom":subQ1}),1.0]])]});}
            var Q71;
            {var subQ1=sQuery(id+"F0.wireOp",EDGE,"E3");var subQ3=sQuery(id+"F0.wireOp",EDGE,"E19");var subQ4=makeQuery(id+"F0.imprint","INTERSECT",VERTEX,{"disambiguationData":[OD(1.0)],"derivedFrom":[subQ1,subQ3]});Q71=makeQuery(id+"F0.imprint","IMPRINT",FACE,{"disambiguationData":[TD([[makeQuery(id+"F0.imprint","IMPRINT",EDGE,{"disambiguationData":[TD([[subQ4,-1.0]])],"derivedFrom":subQ3}),-1.0]])]});}
            extrude(context, id + "F1", {"entities" : qUnion([Q0, Q1, Q2, Q3, Q4, Q5, Q6, Q7, Q8, Q9, Q10, Q11, Q12, Q13, Q14, Q15, Q16, Q17, Q18, Q19, Q20, Q21, Q22, Q23, Q24, Q25, Q26, Q27, Q28, Q29, Q30, Q31, Q32, Q33, Q34, Q35, Q36, Q37, Q38, Q39, Q40, Q41, Q42, Q43, Q44, Q45, Q46, Q47, Q48, Q49, Q50, Q51, Q52, Q53, Q54, Q55, Q56, Q57, Q58, Q59, Q60, Q61, Q62, Q63, Q64, Q65, Q66, Q67, Q68, Q69, Q70, Q71]), "depth" : 2 * mm});
        }
    });
